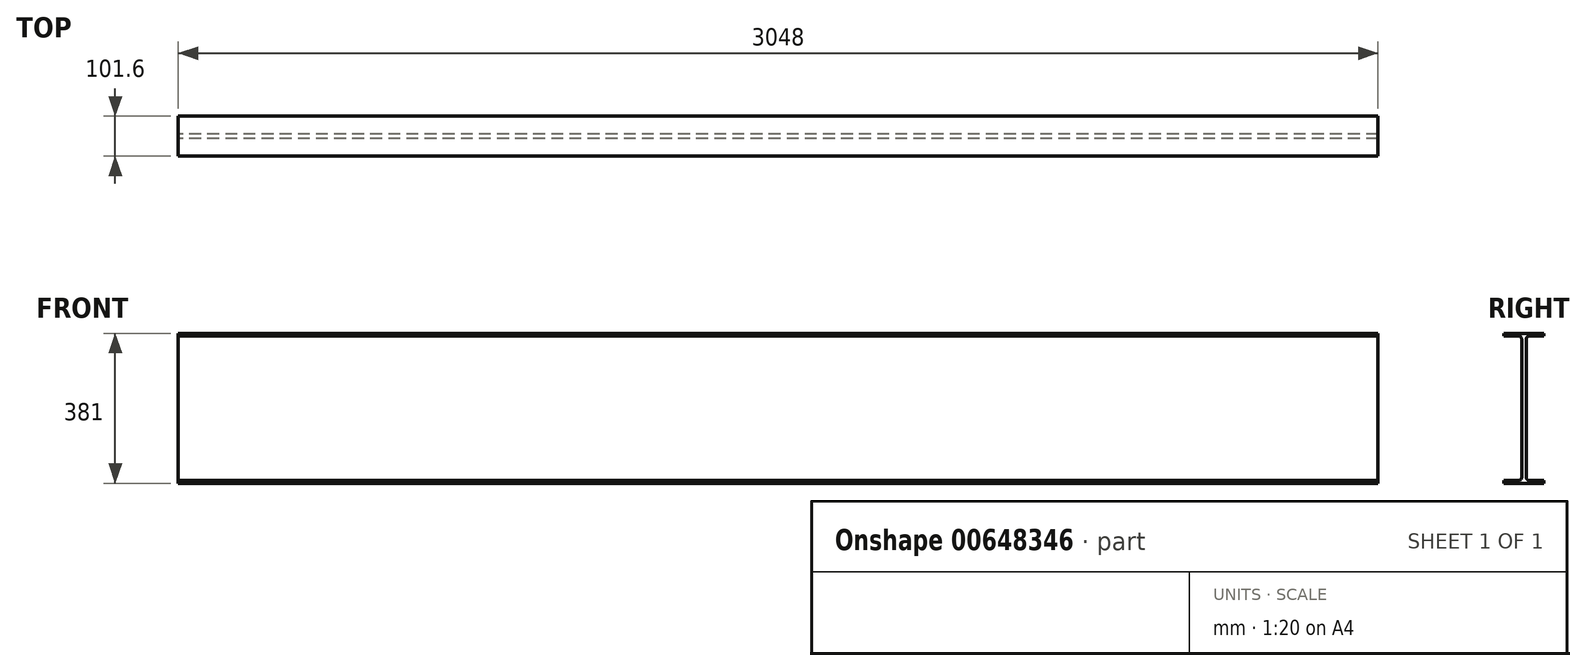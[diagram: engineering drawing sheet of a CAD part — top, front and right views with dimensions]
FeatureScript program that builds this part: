
annotation { "Feature Type Name" : "Feature", "Feature Type Description" : "" }
export const myFeature = defineFeature(function(context is Context, id is Id, definition is map)
    precondition{}
    {
        {
            var Q0;
            Q0=qCreatedBy(makeId("Right.planeOp"),FACE);
            var sketch = newSketch(context, id + "F0", { "sketchPlane" : qUnion([Q0])});
            skLineSegment(sketch, "E0", {"start": v(-5.84, 0) * mm, "end": v(-5.84, 175.73) * mm});
            skLineSegment(sketch, "E1", {"start": v(-13.78, 183.67) * mm, "end": v(-50.8, 183.67) * mm});
            skLineSegment(sketch, "E2", {"start": v(-50.8, 183.67) * mm, "end": v(-50.8, 190.5) * mm});
            skLineSegment(sketch, "E3", {"start": v(-50.8, 190.5) * mm, "end": v(0, 190.5) * mm});
            skPoint(sketch, "E4.visualSharp", {"position": v(-5.84, 183.67) * mm});
            skArc(sketch, "E4.filletArc", {"start": v(-5.84, 175.73) * mm, "mid": v(-8.17, 181.34) * mm, "end": v(-13.78, 183.67) * mm});
            skLineSegment(sketch, "E5.MirrorCS", {"start": v(5.84, 0) * mm, "end": v(5.84, 175.73) * mm});
            skPoint(sketch, "E6.MirrorP", {"position": v(5.84, 183.67) * mm});
            skLineSegment(sketch, "E7.MirrorCS", {"start": v(13.78, 183.67) * mm, "end": v(50.8, 183.67) * mm});
            skArc(sketch, "E8.MirrorCS", {"start": v(5.84, 175.73) * mm, "mid": v(8.17, 181.34) * mm, "end": v(13.78, 183.67) * mm});
            skLineSegment(sketch, "E9.MirrorCS", {"start": v(50.8, 190.5) * mm, "end": v(0, 190.5) * mm});
            skLineSegment(sketch, "E10.MirrorCS", {"start": v(50.8, 183.67) * mm, "end": v(50.8, 190.5) * mm});
            skLineSegment(sketch, "E11.MirrorCS", {"start": v(50.8, -183.67) * mm, "end": v(50.8, -190.5) * mm});
            skLineSegment(sketch, "E12.MirrorCS", {"start": v(-50.8, -183.67) * mm, "end": v(-50.8, -190.5) * mm});
            skArc(sketch, "E13.MirrorCS", {"start": v(5.84, -175.73) * mm, "mid": v(8.17, -181.34) * mm, "end": v(13.78, -183.67) * mm});
            skArc(sketch, "E14.MirrorCS", {"start": v(-5.84, -175.73) * mm, "mid": v(-8.17, -181.34) * mm, "end": v(-13.78, -183.67) * mm});
            skLineSegment(sketch, "E15.MirrorCS", {"start": v(-5.84, 0) * mm, "end": v(-5.84, -175.73) * mm});
            skPoint(sketch, "E16.MirrorP", {"position": v(5.84, -183.67) * mm});
            skLineSegment(sketch, "E17.MirrorCS", {"start": v(-13.78, -183.67) * mm, "end": v(-50.8, -183.67) * mm});
            skPoint(sketch, "E18.MirrorP", {"position": v(-5.84, -183.67) * mm});
            skLineSegment(sketch, "E19.MirrorCS", {"start": v(-50.8, -190.5) * mm, "end": v(0, -190.5) * mm});
            skLineSegment(sketch, "E20.MirrorCS", {"start": v(13.78, -183.67) * mm, "end": v(50.8, -183.67) * mm});
            skLineSegment(sketch, "E21.MirrorCS", {"start": v(50.8, -190.5) * mm, "end": v(0, -190.5) * mm});
            skLineSegment(sketch, "E22.MirrorCS", {"start": v(5.84, 0) * mm, "end": v(5.84, -175.73) * mm});
            skSolve(sketch);
        }
        {
            var Q0;
            Q0=makeQuery(id+"F0.imprint","IMPRINT",FACE,{"disambiguationData":[TD([[makeQuery(id+"F0.imprint","IMPRINT",EDGE,{"derivedFrom":sQuery(id+"F0.wireOp",EDGE,"E0")}),-1.0]])]});
            extrude(context, id + "F1", {"entities" : qUnion([Q0]), "depth" : 3048 * mm, "offsetDistance" : 25.4 * mm});
        }
    });
